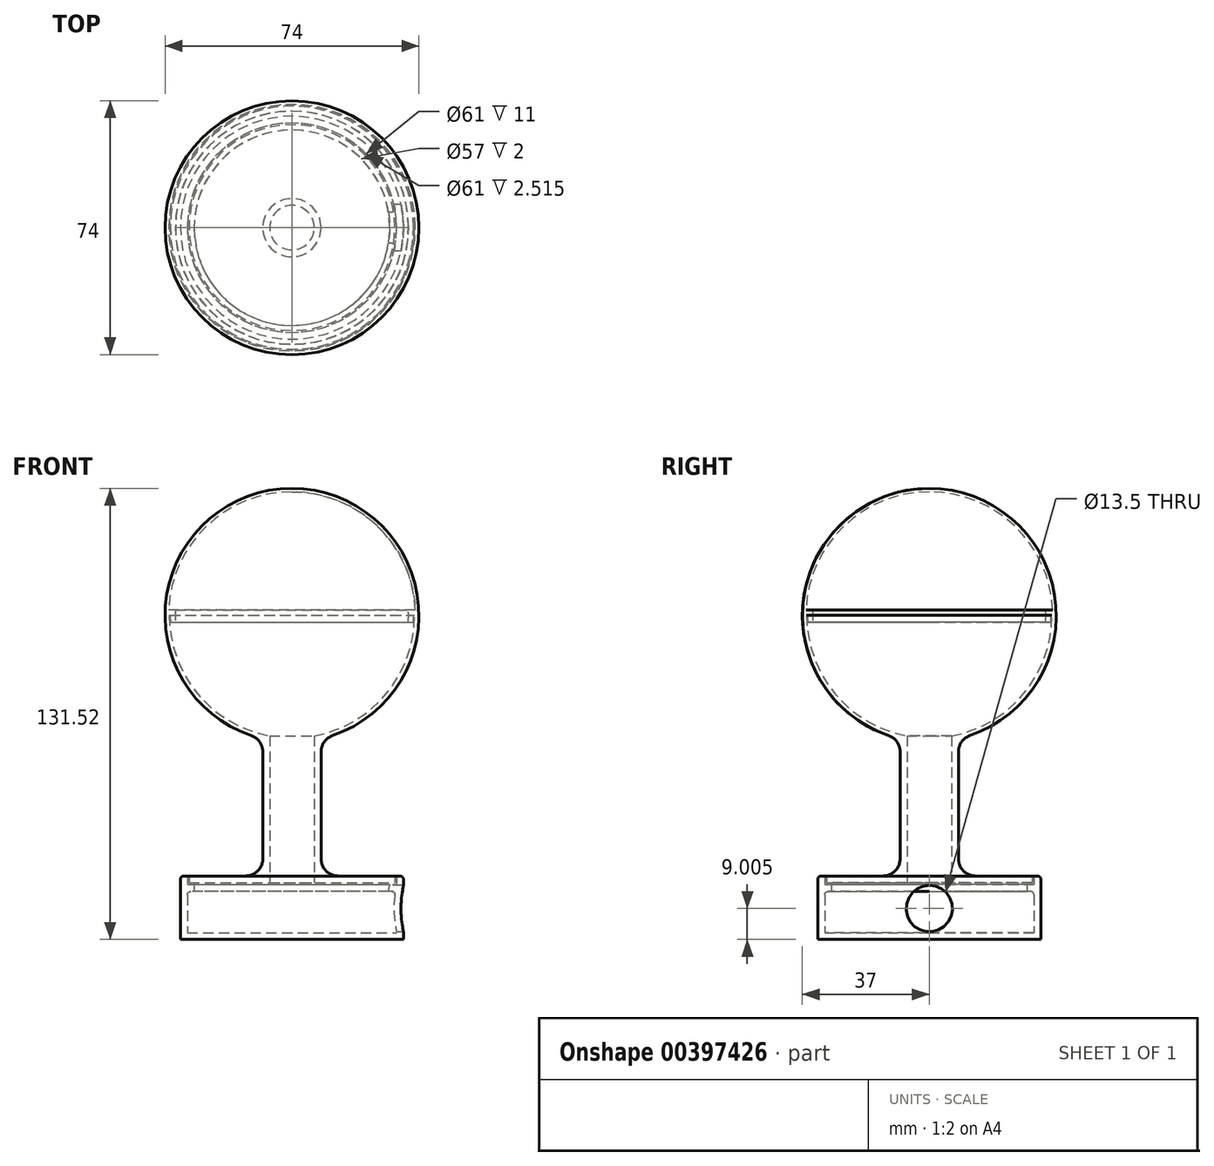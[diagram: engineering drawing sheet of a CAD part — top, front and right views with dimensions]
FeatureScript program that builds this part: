
annotation { "Feature Type Name" : "Feature", "Feature Type Description" : "" }
export const myFeature = defineFeature(function(context is Context, id is Id, definition is map)
    precondition{}
    {
        {
            var Q0;
            Q0=qCreatedBy(makeId("Right.planeOp"),FACE);
            var sketch = newSketch(context, id + "F0", { "sketchPlane" : qUnion([Q0])});
            skLineSegment(sketch, "E0", {"start": v(-13.5, -76) * mm, "end": v(-29.7, -76) * mm});
            skLineSegment(sketch, "E1", {"start": v(-6.5, -75) * mm, "end": v(-6.5, -36.59) * mm});
            skPoint(sketch, "E2.visualSharp", {"position": v(-6.5, -76) * mm});
            skArc(sketch, "E3", {"start": v(-35.75, 0) * mm, "mid": v(-27.48, -22.87) * mm, "end": v(-6.5, -35.15) * mm});
            skArc(sketch, "E4", {"start": v(-37, 0) * mm, "mid": v(-30.08, -21.55) * mm, "end": v(-11.9, -35.04) * mm});
            skLineSegment(sketch, "E5", {"start": v(-37, 0) * mm, "end": v(-35.75, 0) * mm});
            skLineSegment(sketch, "E6", {"start": v(-6.5, -35.15) * mm, "end": v(-6.5, -36.59) * mm});
            skLineSegment(sketch, "E7", {"start": v(-8.5, -39.77) * mm, "end": v(-8.5, -71) * mm});
            skLineSegment(sketch, "E8", {"start": v(-6.5, -76) * mm, "end": v(-6.5, -78) * mm});
            skLineSegment(sketch, "E9", {"start": v(-6.5, -78) * mm, "end": v(-30, -78) * mm});
            skLineSegment(sketch, "E10", {"start": v(-30, -78) * mm, "end": v(-30, -76.3) * mm});
            skLineSegment(sketch, "E11", {"start": v(-6.5, -76) * mm, "end": v(-6.5, -75) * mm});
            skPoint(sketch, "E12.visualSharp", {"position": v(-8.5, -36.01) * mm});
            skArc(sketch, "E12.filletArc", {"start": v(-8.5, -39.77) * mm, "mid": v(-9.44, -36.86) * mm, "end": v(-11.9, -35.04) * mm});
            skPoint(sketch, "E13.visualSharp", {"position": v(-8.5, -76) * mm});
            skArc(sketch, "E13.filletArc", {"start": v(-13.5, -76) * mm, "mid": v(-9.96, -74.54) * mm, "end": v(-8.5, -71) * mm});
            skPoint(sketch, "E14.visualSharp", {"position": v(-30, -76) * mm});
            skArc(sketch, "E14.filletArc", {"start": v(-29.7, -76) * mm, "mid": v(-29.91, -76.09) * mm, "end": v(-30, -76.3) * mm});
            skSolve(sketch);
        }
        {
            var Q0;
            Q0=qCreatedBy(makeId("Right.planeOp"),FACE);
            var sketch = newSketch(context, id + "F1", { "sketchPlane" : qUnion([Q0])});
            skLineSegment(sketch, "E15", {"start": v(0, -75) * mm, "end": v(0, 0) * mm});
            skSolve(sketch);
        }
        {
            var Q0;
            Q0 = qSketchRegion(id + "F0", true);
            var Q1;
            Q1=sQuery(id+"F1.wireOp",EDGE,"E15");
            revolve(context, id + "F2", {"entities" : qUnion([Q0]), "axis" : qUnion([Q1]), "revolveType" : RevolveType.FULL});
        }
        {
            var Q0;
            Q0=qCreatedBy(makeId("Front.planeOp"),FACE);
            var sketch = newSketch(context, id + "F3", { "sketchPlane" : qUnion([Q0])});
            skArc(sketch, "E16", {"start": v(0, 37) * mm, "mid": v(-26.16, 26.16) * mm, "end": v(-37, 0) * mm});
            skArc(sketch, "E17", {"start": v(0, 36) * mm, "mid": v(-25.46, 25.46) * mm, "end": v(-36, 0) * mm});
            skLineSegment(sketch, "E18", {"start": v(-36, 0) * mm, "end": v(-37, 0) * mm});
            skLineSegment(sketch, "E19", {"start": v(0, 36) * mm, "end": v(0, 37) * mm});
            skSolve(sketch);
        }
        {
            var Q0;
            Q0 = qSketchRegion(id + "F3", true);
            var Q1;
            Q1=sQuery(id+"F3.wireOp",EDGE,"E19");
            revolve(context, id + "F4", {"entities" : qUnion([Q0]), "axis" : qUnion([Q1]), "revolveType" : RevolveType.FULL});
        }
        {
            var Q0;
            Q0=qCreatedBy(makeId("Right.planeOp"),FACE);
            var sketch = newSketch(context, id + "F5", { "sketchPlane" : qUnion([Q0])});
            skLineSegment(sketch, "E20", {"start": v(-30.5, -76) * mm, "end": v(-31.5, -76) * mm});
            skLineSegment(sketch, "E21", {"start": v(-30.5, -78.52) * mm, "end": v(-28.5, -78.52) * mm});
            skLineSegment(sketch, "E22", {"start": v(-28.5, -78.52) * mm, "end": v(-28.5, -80.52) * mm});
            skLineSegment(sketch, "E23", {"start": v(-28.5, -80.52) * mm, "end": v(-29.5, -80.52) * mm});
            skLineSegment(sketch, "E24", {"start": v(-30.5, -81.52) * mm, "end": v(-30.5, -92.52) * mm});
            skLineSegment(sketch, "E25", {"start": v(-30.5, -78.52) * mm, "end": v(-30.5, -76) * mm});
            skLineSegment(sketch, "E26", {"start": v(-32.5, -77) * mm, "end": v(-32.5, -92.52) * mm});
            skLineSegment(sketch, "E27", {"start": v(-32.5, -92.52) * mm, "end": v(-32.5, -94.52) * mm});
            skLineSegment(sketch, "E28", {"start": v(-32.5, -94.52) * mm, "end": v(0, -94.52) * mm});
            skLineSegment(sketch, "E29", {"start": v(0, -94.52) * mm, "end": v(0, -92.52) * mm});
            skLineSegment(sketch, "E30", {"start": v(0, -92.52) * mm, "end": v(-30.5, -92.52) * mm});
            skPoint(sketch, "E31.visualSharp", {"position": v(-32.5, -76) * mm});
            skArc(sketch, "E31.filletArc", {"start": v(-31.5, -76) * mm, "mid": v(-32.2, -76.3) * mm, "end": v(-32.5, -77) * mm});
            skPoint(sketch, "E32.visualSharp", {"position": v(-30.5, -80.52) * mm});
            skArc(sketch, "E32.filletArc", {"start": v(-29.5, -80.52) * mm, "mid": v(-30.2, -80.8) * mm, "end": v(-30.5, -81.52) * mm});
            skSolve(sketch);
        }
        {
            var Q0;
            Q0 = qSketchRegion(id + "F5", true);
            var Q1;
            Q1=sQuery(id+"F5.wireOp",EDGE,"E29");
            revolve(context, id + "F6", {"entities" : qUnion([Q0]), "axis" : qUnion([Q1]), "revolveType" : RevolveType.FULL});
        }
        {
            var Q0;
            Q0=qCreatedBy(makeId("Right.planeOp"),FACE);
            var sketch = newSketch(context, id + "F7", { "sketchPlane" : qUnion([Q0])});
            skCircle(sketch, "E33", {"center": v(0, -85.52) * mm, "radius": 6.75 * mm});
            skSolve(sketch);
        }
        {
            var Q0;
            Q0 = qSketchRegion(id + "F7", true);
            extrude(context, id + "F8", {"entities" : qUnion([Q0]), "operationType" : NewBodyOperationType.REMOVE, "depth" : 50 * mm});
        }
        {
            var Q0;
            Q0=qCreatedBy(makeId("Front.planeOp"),FACE);
            var sketch = newSketch(context, id + "F9", { "sketchPlane" : qUnion([Q0])});
            skArc(sketch, "E34", {"start": v(-35.5, 0) * mm, "mid": v(-35.49, -1) * mm, "end": v(-35.44, -2) * mm});
            skArc(sketch, "E35", {"start": v(-33.97, 1.5) * mm, "mid": v(-34, -0.25) * mm, "end": v(-33.94, -2) * mm});
            skLineSegment(sketch, "E36", {"start": v(-36.1, 0) * mm, "end": v(-36.1, 1.5) * mm});
            skLineSegment(sketch, "E37", {"start": v(-36.1, 1.5) * mm, "end": v(-33.97, 1.5) * mm});
            skLineSegment(sketch, "E38", {"start": v(-35.44, -2) * mm, "end": v(-33.94, -2) * mm});
            skLineSegment(sketch, "E39", {"start": v(-36.1, 0) * mm, "end": v(-35.5, 0) * mm});
            skSolve(sketch);
        }
        {
            var Q0;
            Q0 = qSketchRegion(id + "F9", true);
            var Q1;
            Q1=sQuery(id+"F1.wireOp",EDGE,"E15");
            revolve(context, id + "F10", {"operationType" : NewBodyOperationType.ADD, "entities" : qUnion([Q0]), "axis" : qUnion([Q1]), "revolveType" : RevolveType.FULL});
        }
    });
